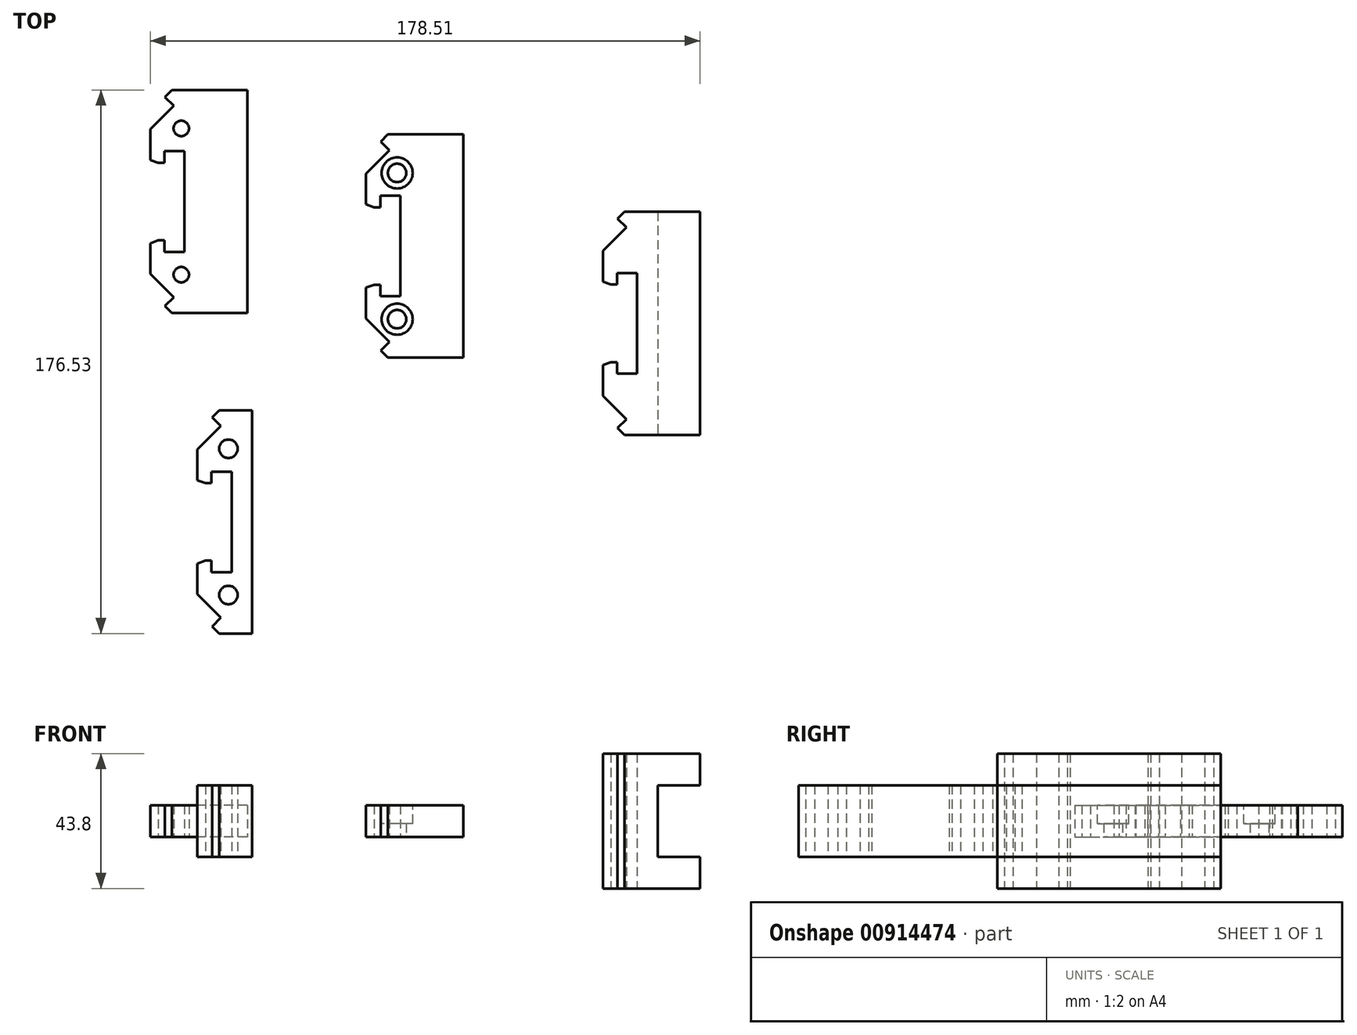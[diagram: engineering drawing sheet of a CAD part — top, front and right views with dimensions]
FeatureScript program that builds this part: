
annotation { "Feature Type Name" : "Feature", "Feature Type Description" : "" }
export const myFeature = defineFeature(function(context is Context, id is Id, definition is map)
    precondition{}
    {
        {
            var Q0;
            Q0=qCreatedBy(makeId("Top.planeOp"),FACE);
            var sketch = newSketch(context, id + "F0", { "sketchPlane" : qUnion([Q0])});
            skLineSegment(sketch, "E0.bottom", {"start": v(12.25, -36.25) * mm, "end": v(-12.25, -36.25) * mm});
            skLineSegment(sketch, "E0.top", {"start": v(12.25, 36.25) * mm, "end": v(-12.25, 36.25) * mm});
            skLineSegment(sketch, "E0.left", {"start": v(12.25, -36.25) * mm, "end": v(12.25, 36.25) * mm});
            skPoint(sketch, "E0.middle", {"position": v(0, 0) * mm});
            skLineSegment(sketch, "E1", {"start": v(-12.25, 36.25) * mm, "end": v(-14.55, 33.95) * mm});
            skLineSegment(sketch, "E2", {"start": v(-14.55, 33.95) * mm, "end": v(-11.72, 31.12) * mm});
            skLineSegment(sketch, "E3", {"start": v(-11.72, 31.12) * mm, "end": v(-19.32, 23.52) * mm});
            skLineSegment(sketch, "E4", {"start": v(-19.32, 23.52) * mm, "end": v(-19.32, 13.52) * mm});
            skLineSegment(sketch, "E5", {"start": v(-14.73, 13.32) * mm, "end": v(-14.73, 16.34) * mm});
            skLineSegment(sketch, "E6", {"start": v(-14.73, 16.34) * mm, "end": v(-8.23, 16.34) * mm});
            skLineSegment(sketch, "E7", {"start": v(-8.23, 16.34) * mm, "end": v(-8.23, 0) * mm});
            skLineSegment(sketch, "E8", {"start": v(-19.32, 13.52) * mm, "end": v(-16.73, 12.59) * mm});
            skLineSegment(sketch, "E9", {"start": v(-16.73, 12.59) * mm, "end": v(-14.73, 12.59) * mm});
            skLineSegment(sketch, "E10", {"start": v(-14.73, 12.59) * mm, "end": v(-14.73, 13.32) * mm});
            skLineSegment(sketch, "E11.MirrorCS", {"start": v(-8.23, -16.34) * mm, "end": v(-8.23, 0) * mm});
            skLineSegment(sketch, "E12.MirrorCS", {"start": v(-14.73, -16.34) * mm, "end": v(-8.23, -16.34) * mm});
            skLineSegment(sketch, "E13.MirrorCS", {"start": v(-14.73, -12.59) * mm, "end": v(-14.73, -13.32) * mm});
            skLineSegment(sketch, "E14.MirrorCS", {"start": v(-19.32, -13.52) * mm, "end": v(-16.73, -12.59) * mm});
            skLineSegment(sketch, "E15.MirrorCS", {"start": v(-16.73, -12.59) * mm, "end": v(-14.73, -12.59) * mm});
            skLineSegment(sketch, "E16.MirrorCS", {"start": v(-19.32, -23.52) * mm, "end": v(-19.32, -13.52) * mm});
            skLineSegment(sketch, "E17.MirrorCS", {"start": v(-14.73, -13.32) * mm, "end": v(-14.73, -16.34) * mm});
            skLineSegment(sketch, "E18.MirrorCS", {"start": v(-11.72, -31.12) * mm, "end": v(-19.32, -23.52) * mm});
            skLineSegment(sketch, "E19.MirrorCS", {"start": v(-14.55, -33.95) * mm, "end": v(-11.72, -31.12) * mm});
            skLineSegment(sketch, "E20.MirrorCS", {"start": v(-12.25, -36.25) * mm, "end": v(-14.55, -33.95) * mm});
            skSolve(sketch);
        }
        {
            var Q0;
            Q0 = qSketchRegion(id + "F0", true);
            extrude(context, id + "F1", {"entities" : qUnion([Q0]), "endBound" : BoundingType.SYMMETRIC, "depth" : 43.8 * mm, "offsetDistance" : 25 * mm});
        }
        {
            var Q0;
            Q0=makeQuery(id+"F1.opExtrude","SWEPT_FACE",FACE,{"disambiguationData":[OSD([sQuery(id+"F0.wireOp",EDGE,"E0.left")])]});
            var sketch = newSketch(context, id + "F2", { "sketchPlane" : qUnion([Q0])});
            skLineSegment(sketch, "E21.bottom", {"start": v(36.25, -11.6) * mm, "end": v(-36.25, -11.6) * mm});
            skLineSegment(sketch, "E21.top", {"start": v(36.25, 11.6) * mm, "end": v(-36.25, 11.6) * mm});
            skLineSegment(sketch, "E21.left", {"start": v(36.25, -11.6) * mm, "end": v(36.25, 11.6) * mm});
            skLineSegment(sketch, "E21.right", {"start": v(-36.25, -11.6) * mm, "end": v(-36.25, 11.6) * mm});
            skPoint(sketch, "E21.middle", {"position": v(0, 0) * mm});
            skSolve(sketch);
        }
        {
            var Q0;
            Q0 = qSketchRegion(id + "F2", true);
            extrude(context, id + "F3", {"entities" : qUnion([Q0]), "operationType" : NewBodyOperationType.REMOVE, "oppositeDirection" : true, "depth" : 13.8 * mm, "offsetDistance" : 25 * mm});
        }
        {
            var Q0;
            Q0=qCreatedBy(makeId("Top.planeOp"),FACE);
            var sketch = newSketch(context, id + "F4", { "sketchPlane" : qUnion([Q0])});
            skLineSegment(sketch, "E22.bottom", {"start": v(-64.62, -11.15) * mm, "end": v(-89.12, -11.15) * mm});
            skLineSegment(sketch, "E22.top", {"start": v(-64.62, 61.35) * mm, "end": v(-89.12, 61.35) * mm});
            skLineSegment(sketch, "E22.left", {"start": v(-64.62, -11.15) * mm, "end": v(-64.62, 61.35) * mm});
            skPoint(sketch, "E22.middle", {"position": v(-76.87, 25.1) * mm});
            skLineSegment(sketch, "E23", {"start": v(-89.12, 61.35) * mm, "end": v(-91.41, 59.05) * mm});
            skLineSegment(sketch, "E24", {"start": v(-91.41, 59.05) * mm, "end": v(-88.59, 56.22) * mm});
            skLineSegment(sketch, "E25", {"start": v(-88.59, 56.22) * mm, "end": v(-96.19, 48.62) * mm});
            skLineSegment(sketch, "E26", {"start": v(-96.19, 48.62) * mm, "end": v(-96.19, 38.62) * mm});
            skLineSegment(sketch, "E27", {"start": v(-91.6, 38.42) * mm, "end": v(-91.6, 41.44) * mm});
            skLineSegment(sketch, "E28", {"start": v(-91.6, 41.44) * mm, "end": v(-85.1, 41.44) * mm});
            skLineSegment(sketch, "E29", {"start": v(-85.1, 41.44) * mm, "end": v(-85.1, 25.1) * mm});
            skLineSegment(sketch, "E30", {"start": v(-96.19, 38.62) * mm, "end": v(-93.6, 37.69) * mm});
            skLineSegment(sketch, "E31", {"start": v(-93.6, 37.69) * mm, "end": v(-91.6, 37.69) * mm});
            skLineSegment(sketch, "E32", {"start": v(-91.6, 37.69) * mm, "end": v(-91.6, 38.42) * mm});
            skLineSegment(sketch, "E33.MirrorCS", {"start": v(-85.1, 8.76) * mm, "end": v(-85.1, 25.1) * mm});
            skLineSegment(sketch, "E34.MirrorCS", {"start": v(-91.6, 8.76) * mm, "end": v(-85.1, 8.76) * mm});
            skLineSegment(sketch, "E35.MirrorCS", {"start": v(-91.6, 12.51) * mm, "end": v(-91.6, 11.78) * mm});
            skLineSegment(sketch, "E36.MirrorCS", {"start": v(-96.19, 11.58) * mm, "end": v(-93.6, 12.51) * mm});
            skLineSegment(sketch, "E37.MirrorCS", {"start": v(-93.6, 12.51) * mm, "end": v(-91.6, 12.51) * mm});
            skLineSegment(sketch, "E38.MirrorCS", {"start": v(-96.19, 1.58) * mm, "end": v(-96.19, 11.58) * mm});
            skLineSegment(sketch, "E39.MirrorCS", {"start": v(-91.6, 11.78) * mm, "end": v(-91.6, 8.76) * mm});
            skLineSegment(sketch, "E40.MirrorCS", {"start": v(-88.59, -6.02) * mm, "end": v(-96.19, 1.58) * mm});
            skLineSegment(sketch, "E41.MirrorCS", {"start": v(-91.41, -8.85) * mm, "end": v(-88.59, -6.02) * mm});
            skLineSegment(sketch, "E42.MirrorCS", {"start": v(-89.12, -11.15) * mm, "end": v(-91.41, -8.85) * mm});
            skLineSegment(sketch, "E43.bottom", {"start": v(-134.7, 3.3) * mm, "end": v(-159.2, 3.3) * mm});
            skLineSegment(sketch, "E43.top", {"start": v(-134.7, 75.8) * mm, "end": v(-159.2, 75.8) * mm});
            skLineSegment(sketch, "E43.left", {"start": v(-134.7, 3.3) * mm, "end": v(-134.7, 75.8) * mm});
            skPoint(sketch, "E43.middle", {"position": v(-146.94, 39.55) * mm});
            skLineSegment(sketch, "E44", {"start": v(-159.2, 75.8) * mm, "end": v(-161.5, 73.5) * mm});
            skLineSegment(sketch, "E45", {"start": v(-161.5, 73.5) * mm, "end": v(-158.66, 70.68) * mm});
            skLineSegment(sketch, "E46", {"start": v(-158.66, 70.68) * mm, "end": v(-166.26, 63.08) * mm});
            skLineSegment(sketch, "E47", {"start": v(-166.26, 63.08) * mm, "end": v(-166.26, 53.08) * mm});
            skLineSegment(sketch, "E48", {"start": v(-161.68, 52.88) * mm, "end": v(-161.68, 55.9) * mm});
            skLineSegment(sketch, "E49", {"start": v(-161.68, 55.9) * mm, "end": v(-155.18, 55.9) * mm});
            skLineSegment(sketch, "E50", {"start": v(-155.18, 55.9) * mm, "end": v(-155.18, 39.55) * mm});
            skLineSegment(sketch, "E51", {"start": v(-166.26, 53.08) * mm, "end": v(-163.68, 52.14) * mm});
            skLineSegment(sketch, "E52", {"start": v(-163.68, 52.14) * mm, "end": v(-161.68, 52.14) * mm});
            skLineSegment(sketch, "E53", {"start": v(-161.68, 52.14) * mm, "end": v(-161.68, 52.88) * mm});
            skLineSegment(sketch, "E54.MirrorCS", {"start": v(-155.18, 23.22) * mm, "end": v(-155.18, 39.55) * mm});
            skLineSegment(sketch, "E55.MirrorCS", {"start": v(-161.68, 23.22) * mm, "end": v(-155.18, 23.22) * mm});
            skLineSegment(sketch, "E56.MirrorCS", {"start": v(-161.68, 26.97) * mm, "end": v(-161.68, 26.23) * mm});
            skLineSegment(sketch, "E57.MirrorCS", {"start": v(-166.26, 26.03) * mm, "end": v(-163.68, 26.97) * mm});
            skLineSegment(sketch, "E58.MirrorCS", {"start": v(-163.68, 26.97) * mm, "end": v(-161.68, 26.97) * mm});
            skLineSegment(sketch, "E59.MirrorCS", {"start": v(-166.26, 16.03) * mm, "end": v(-166.26, 26.03) * mm});
            skLineSegment(sketch, "E60.MirrorCS", {"start": v(-161.68, 26.23) * mm, "end": v(-161.68, 23.22) * mm});
            skLineSegment(sketch, "E61.MirrorCS", {"start": v(-158.66, 8.43) * mm, "end": v(-166.26, 16.03) * mm});
            skLineSegment(sketch, "E62.MirrorCS", {"start": v(-161.5, 5.6) * mm, "end": v(-158.66, 8.43) * mm});
            skLineSegment(sketch, "E63.MirrorCS", {"start": v(-159.2, 3.3) * mm, "end": v(-161.5, 5.6) * mm});
            skCircle(sketch, "E64", {"center": v(-156.2, 63.3) * mm, "radius": 2.5 * mm});
            skCircle(sketch, "E65", {"center": v(-156.2, 15.8) * mm, "radius": 2.5 * mm});
            skCircle(sketch, "E66", {"center": v(-86.12, 48.85) * mm, "radius": 3 * mm});
            skCircle(sketch, "E67", {"center": v(-86.12, 1.35) * mm, "radius": 3 * mm});
            skSolve(sketch);
        }
        {
            var Q0;
            Q0 = qSketchRegion(id + "F4", true);
            extrude(context, id + "F5", {"entities" : qUnion([Q0]), "endBound" : BoundingType.SYMMETRIC, "depth" : 10.3 * mm, "offsetDistance" : 25 * mm});
        }
        {
            var Q0;
            Q0=qCreatedBy(makeId("Top.planeOp"),FACE);
            var sketch = newSketch(context, id + "F6", { "sketchPlane" : qUnion([Q0])});
            skLineSegment(sketch, "E68.bottom", {"start": v(-133.18, -100.73) * mm, "end": v(-143.88, -100.73) * mm});
            skLineSegment(sketch, "E68.top", {"start": v(-133.18, -28.23) * mm, "end": v(-143.88, -28.23) * mm});
            skPoint(sketch, "E68.middle", {"position": v(-131.63, -64.48) * mm});
            skLineSegment(sketch, "E69", {"start": v(-143.88, -28.23) * mm, "end": v(-146.18, -30.53) * mm});
            skLineSegment(sketch, "E70", {"start": v(-146.18, -30.53) * mm, "end": v(-143.35, -33.36) * mm});
            skLineSegment(sketch, "E71", {"start": v(-143.35, -33.36) * mm, "end": v(-150.95, -40.96) * mm});
            skLineSegment(sketch, "E72", {"start": v(-150.95, -40.96) * mm, "end": v(-150.95, -50.96) * mm});
            skLineSegment(sketch, "E73", {"start": v(-146.36, -51.16) * mm, "end": v(-146.36, -48.14) * mm});
            skLineSegment(sketch, "E74", {"start": v(-146.36, -48.14) * mm, "end": v(-139.86, -48.14) * mm});
            skLineSegment(sketch, "E75", {"start": v(-139.86, -48.14) * mm, "end": v(-139.86, -64.48) * mm});
            skLineSegment(sketch, "E76", {"start": v(-150.95, -50.96) * mm, "end": v(-148.36, -51.9) * mm});
            skLineSegment(sketch, "E77", {"start": v(-148.36, -51.9) * mm, "end": v(-146.36, -51.9) * mm});
            skLineSegment(sketch, "E78", {"start": v(-146.36, -51.9) * mm, "end": v(-146.36, -51.16) * mm});
            skLineSegment(sketch, "E79.MirrorCS", {"start": v(-139.86, -80.82) * mm, "end": v(-139.86, -64.48) * mm});
            skLineSegment(sketch, "E80.MirrorCS", {"start": v(-146.36, -80.82) * mm, "end": v(-139.86, -80.82) * mm});
            skLineSegment(sketch, "E81.MirrorCS", {"start": v(-146.36, -77.07) * mm, "end": v(-146.36, -77.8) * mm});
            skLineSegment(sketch, "E82.MirrorCS", {"start": v(-150.95, -78) * mm, "end": v(-148.36, -77.07) * mm});
            skLineSegment(sketch, "E83.MirrorCS", {"start": v(-148.36, -77.07) * mm, "end": v(-146.36, -77.07) * mm});
            skLineSegment(sketch, "E84.MirrorCS", {"start": v(-150.95, -88) * mm, "end": v(-150.95, -78) * mm});
            skLineSegment(sketch, "E85.MirrorCS", {"start": v(-146.36, -77.8) * mm, "end": v(-146.36, -80.82) * mm});
            skLineSegment(sketch, "E86.MirrorCS", {"start": v(-143.35, -95.6) * mm, "end": v(-150.95, -88) * mm});
            skLineSegment(sketch, "E87.MirrorCS", {"start": v(-146.18, -98.43) * mm, "end": v(-143.35, -95.6) * mm});
            skLineSegment(sketch, "E88.MirrorCS", {"start": v(-143.88, -100.73) * mm, "end": v(-146.18, -98.43) * mm});
            skLineSegment(sketch, "E89", {"start": v(-133.18, -28.23) * mm, "end": v(-133.18, -100.73) * mm});
            skPoint(sketch, "E89.endSnap0", {"position": v(-131.63, -100.73) * mm});
            skPoint(sketch, "E68.left.end.orphan", {"position": v(-119.38, -28.23) * mm});
            skPoint(sketch, "E90.orphan", {"position": v(-119.38, -100.73) * mm});
            skLineSegment(sketch, "E91", {"start": v(-119.38, -28.23) * mm, "end": v(-119.38, -100.73) * mm, "construction": true});
            skCircle(sketch, "E92", {"center": v(-140.88, -40.73) * mm, "radius": 3 * mm});
            skCircle(sketch, "E93", {"center": v(-140.88, -88.23) * mm, "radius": 3 * mm});
            skSolve(sketch);
        }
        {
            var Q0;
            Q0=makeQuery(id+"F6.imprint","IMPRINT",FACE,{"disambiguationData":[TD([[makeQuery(id+"F6.imprint","IMPRINT",EDGE,{"derivedFrom":sQuery(id+"F6.wireOp",EDGE,"E68.bottom")}),-1.0]])]});
            extrude(context, id + "F7", {"entities" : qUnion([Q0]), "endBound" : BoundingType.SYMMETRIC, "depth" : 23.2 * mm, "offsetDistance" : 25 * mm});
        }
        {
            var Q0;
            Q0=makeQuery(id+"F5.opExtrude","CAP_FACE",FACE,{"disambiguationData":[OSD([sQuery(id+"F4.wireOp",EDGE,"E22.bottom"),sQuery(id+"F4.wireOp",EDGE,"E22.top"),sQuery(id+"F4.wireOp",EDGE,"E22.left"),sQuery(id+"F4.wireOp",EDGE,"E23"),sQuery(id+"F4.wireOp",EDGE,"E24"),sQuery(id+"F4.wireOp",EDGE,"E25"),sQuery(id+"F4.wireOp",EDGE,"E26"),sQuery(id+"F4.wireOp",EDGE,"E27"),sQuery(id+"F4.wireOp",EDGE,"E28"),sQuery(id+"F4.wireOp",EDGE,"E29"),sQuery(id+"F4.wireOp",EDGE,"E30"),sQuery(id+"F4.wireOp",EDGE,"E31"),sQuery(id+"F4.wireOp",EDGE,"E32"),sQuery(id+"F4.wireOp",EDGE,"E33.MirrorCS"),sQuery(id+"F4.wireOp",EDGE,"E35.MirrorCS"),sQuery(id+"F4.wireOp",EDGE,"E36.MirrorCS"),sQuery(id+"F4.wireOp",EDGE,"E37.MirrorCS"),sQuery(id+"F4.wireOp",EDGE,"E38.MirrorCS"),sQuery(id+"F4.wireOp",EDGE,"E34.MirrorCS"),sQuery(id+"F4.wireOp",EDGE,"E39.MirrorCS"),sQuery(id+"F4.wireOp",EDGE,"E40.MirrorCS"),sQuery(id+"F4.wireOp",EDGE,"E41.MirrorCS"),sQuery(id+"F4.wireOp",EDGE,"E42.MirrorCS"),sQuery(id+"F4.wireOp",EDGE,"E66"),sQuery(id+"F4.wireOp",EDGE,"E67")])],"isStart":false});
            var sketch = newSketch(context, id + "F8", { "sketchPlane" : qUnion([Q0])});
            skCircle(sketch, "E94", {"center": v(-86.12, 48.85) * mm, "radius": 5.05 * mm});
            skCircle(sketch, "E95", {"center": v(-86.12, 1.35) * mm, "radius": 5.05 * mm});
            skSolve(sketch);
        }
        {
            var Q0;
            Q0 = qSketchRegion(id + "F8", true);
            extrude(context, id + "F9", {"entities" : qUnion([Q0]), "operationType" : NewBodyOperationType.REMOVE, "oppositeDirection" : true, "depth" : 6 * mm, "offsetDistance" : 25 * mm});
        }
    });
